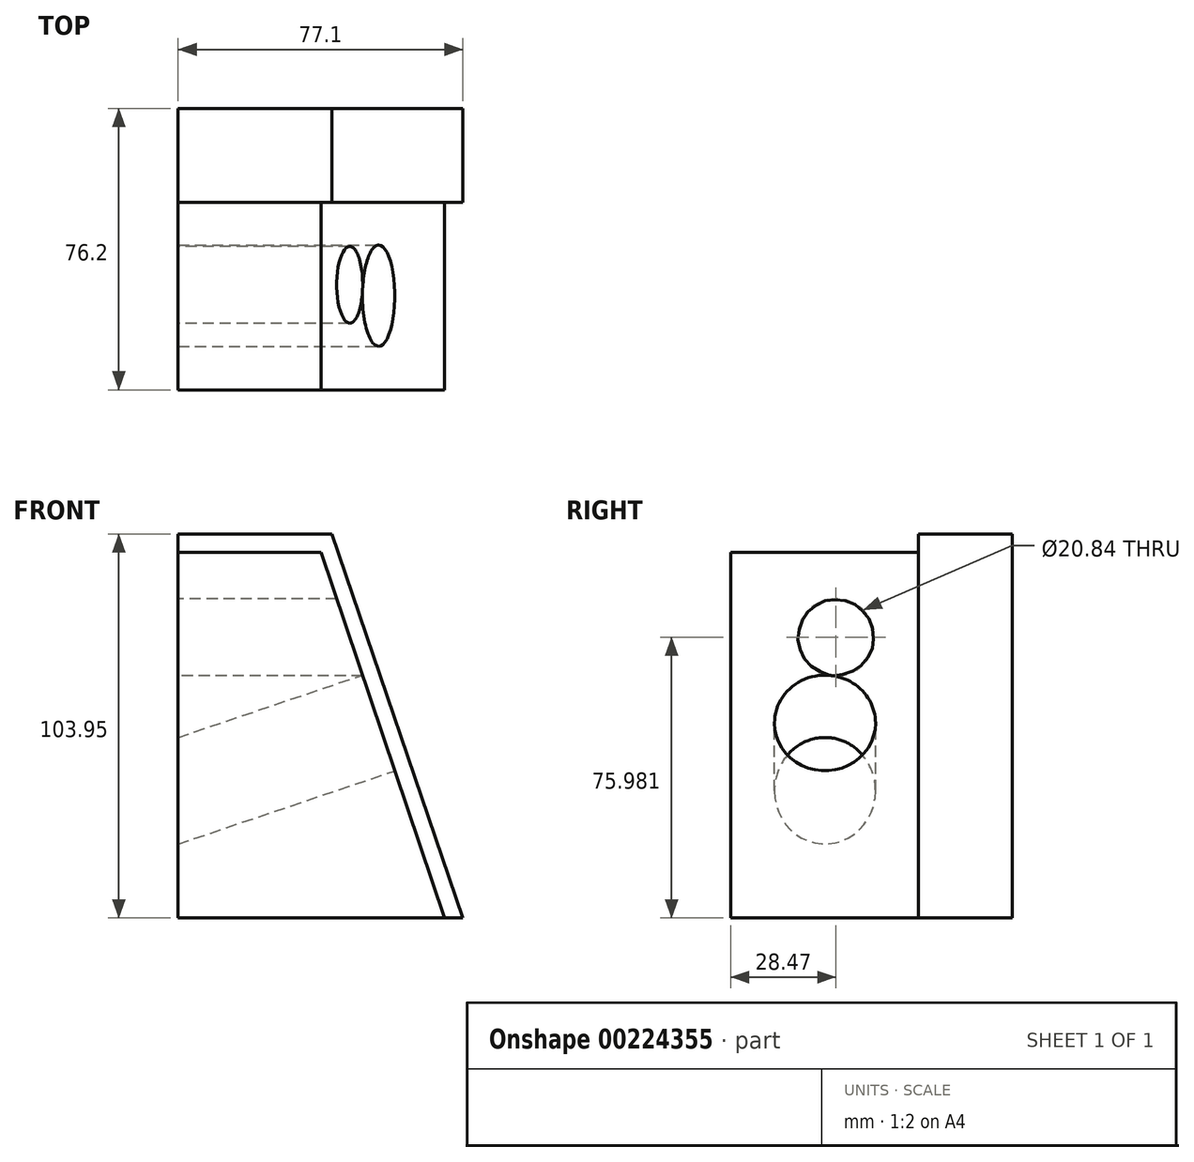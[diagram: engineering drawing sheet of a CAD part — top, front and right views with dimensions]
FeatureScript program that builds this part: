
annotation { "Feature Type Name" : "Feature", "Feature Type Description" : "" }
export const myFeature = defineFeature(function(context is Context, id is Id, definition is map)
    precondition{}
    {
        {
            var Q0;
            Q0=qCreatedBy(makeId("Front.planeOp"),FACE);
            var sketch = newSketch(context, id + "F0", { "sketchPlane" : qUnion([Q0])});
            skLineSegment(sketch, "E0.bottom", {"start": v(2.6, 49.52) * mm, "end": v(-36.07, 49.52) * mm});
            skLineSegment(sketch, "E0.top", {"start": v(36.07, -49.52) * mm, "end": v(-36.07, -49.52) * mm});
            skLineSegment(sketch, "E0.right", {"start": v(-36.07, 49.52) * mm, "end": v(-36.07, -49.52) * mm});
            skPoint(sketch, "E0.middle", {"position": v(0, 0) * mm});
            skLineSegment(sketch, "E1.bottom", {"start": v(-36.07, -49.52) * mm, "end": v(41.03, -49.52) * mm});
            skLineSegment(sketch, "E1.left", {"start": v(-36.07, -49.52) * mm, "end": v(-36.07, 54.43) * mm});
            skLineSegment(sketch, "E2", {"start": v(2.6, 49.52) * mm, "end": v(36.07, -49.52) * mm});
            skPoint(sketch, "E0.left.start.orphan", {"position": v(36.07, 49.52) * mm});
            skLineSegment(sketch, "E3", {"start": v(41.03, -49.52) * mm, "end": v(5.56, 54.43) * mm});
            skLineSegment(sketch, "E4", {"start": v(5.56, 54.43) * mm, "end": v(-36.07, 54.43) * mm});
            skSolve(sketch);
        }
        {
            var Q0;
            {var subQ0=sQuery(id+"F0.wireOp",EDGE,"E0.bottom");Q0=makeQuery(id+"F0.imprint","IMPRINT",FACE,{"disambiguationData":[TD([[makeQuery(id+"F0.imprint","IMPRINT",EDGE,{"derivedFrom":subQ0}),1.0]])]});}
            extrude(context, id + "F1", {"entities" : qUnion([Q0]), "depth" : 76.2 * mm});
        }
        {
            var Q0;
            Q0 = qSketchRegion(id + "F0", true);
            extrude(context, id + "F2", {"entities" : qUnion([Q0]), "operationType" : NewBodyOperationType.ADD, "depth" : 25.4 * mm});
        }
        {
            var Q0;
            Q0=makeQuery(id+"F1.opExtrude","SWEPT_FACE",FACE,{"disambiguationData":[OSD([sQuery(id+"F0.wireOp",EDGE,"E2")])]});
            var sketch = newSketch(context, id + "F3", { "sketchPlane" : qUnion([Q0])});
            skCircle(sketch, "E5", {"center": v(-50.69, -2.73) * mm, "radius": 13.67 * mm});
            skSolve(sketch);
        }
        {
            var Q0;
            Q0 = qSketchRegion(id + "F3", true);
            extrude(context, id + "F4", {"entities" : qUnion([Q0]), "operationType" : NewBodyOperationType.REMOVE, "oppositeDirection" : true, "depth" : 120.65 * mm});
        }
        {
            var Q0;
            Q0=qCreatedBy(makeId("Right.planeOp"),FACE);
            var sketch = newSketch(context, id + "F5", { "sketchPlane" : qUnion([Q0])});
            skCircle(sketch, "E6", {"center": v(-47.73, 26.46) * mm, "radius": 10.42 * mm});
            skSolve(sketch);
        }
        {
            var Q0;
            Q0 = qSketchRegion(id + "F5", true);
            extrude(context, id + "F6", {"entities" : qUnion([Q0]), "operationType" : NewBodyOperationType.REMOVE, "depth" : 108.2 * mm, "hasSecondDirection" : true, "secondDirectionOppositeDirection" : true, "secondDirectionDepth" : 97.03 * mm});
        }
    });
